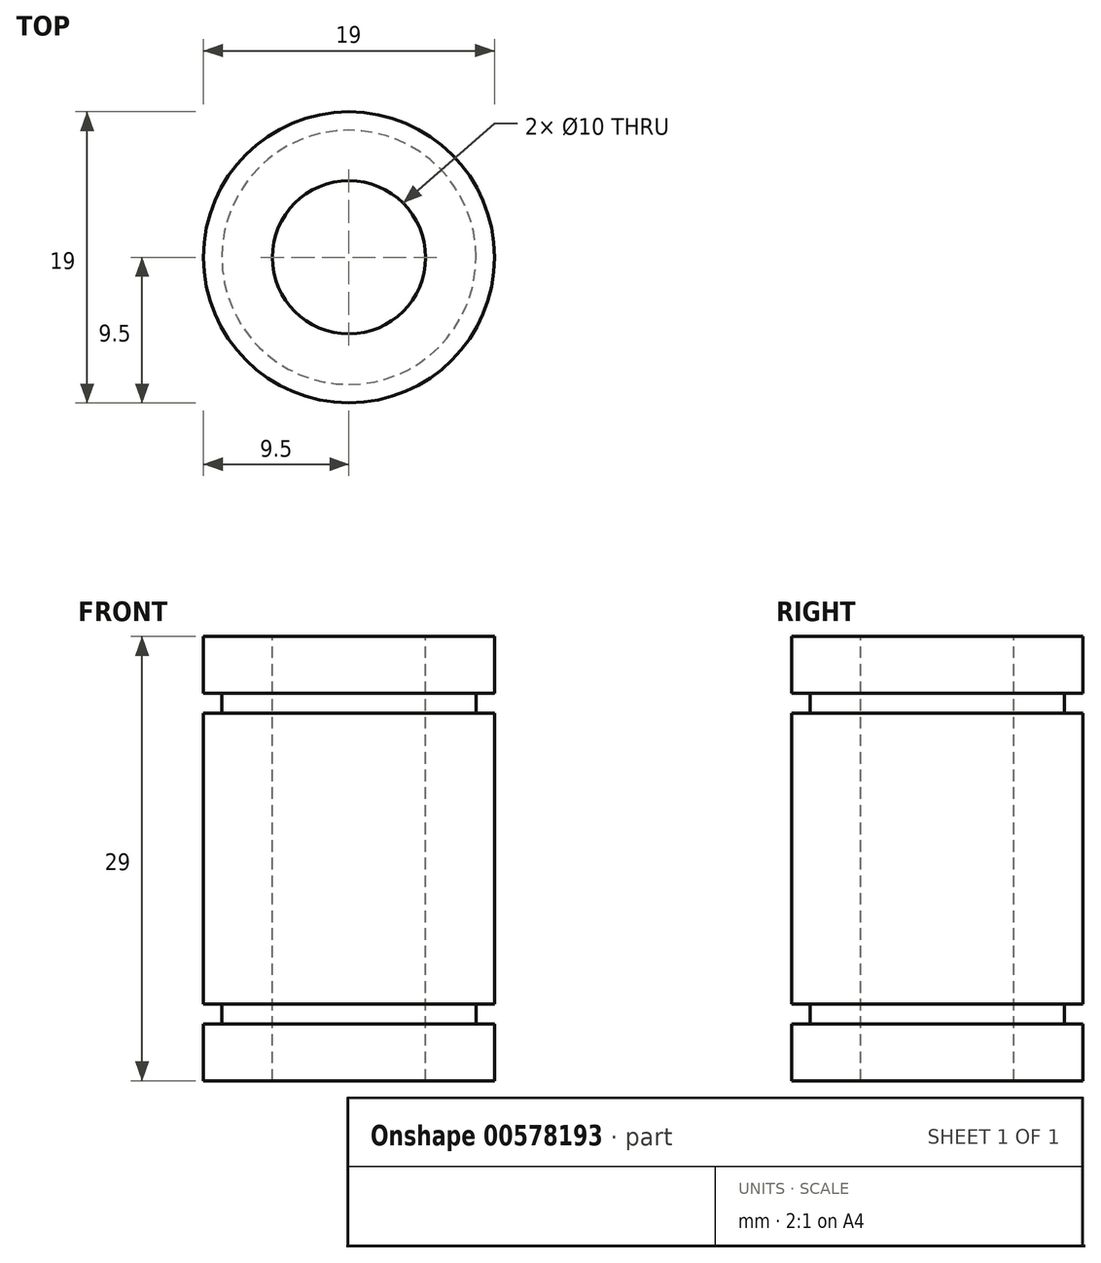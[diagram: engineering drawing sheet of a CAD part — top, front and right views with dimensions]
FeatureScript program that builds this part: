
annotation { "Feature Type Name" : "Feature", "Feature Type Description" : "" }
export const myFeature = defineFeature(function(context is Context, id is Id, definition is map)
    precondition{}
    {
        {
            var Q0;
            Q0=qCreatedBy(makeId("Front.planeOp"),FACE);
            var sketch = newSketch(context, id + "F0", { "sketchPlane" : qUnion([Q0])});
            skLineSegment(sketch, "E0", {"start": v(0, 14.5) * mm, "end": v(-9.5, 14.5) * mm});
            skLineSegment(sketch, "E1", {"start": v(-9.5, 14.5) * mm, "end": v(-9.5, 10.8) * mm});
            skLineSegment(sketch, "E2", {"start": v(-9.5, 10.8) * mm, "end": v(-8.3, 10.8) * mm});
            skLineSegment(sketch, "E3", {"start": v(-8.3, 10.8) * mm, "end": v(-8.3, 9.5) * mm});
            skLineSegment(sketch, "E4", {"start": v(-8.3, 9.5) * mm, "end": v(-9.5, 9.5) * mm});
            skLineSegment(sketch, "E5", {"start": v(-9.5, 9.5) * mm, "end": v(-9.5, 0) * mm});
            skLineSegment(sketch, "E6", {"start": v(-24.14, 0) * mm, "end": v(24.62, 0) * mm, "construction": true});
            skLineSegment(sketch, "E7.MirrorCS", {"start": v(0, -14.5) * mm, "end": v(-9.5, -14.5) * mm});
            skLineSegment(sketch, "E8.MirrorCS", {"start": v(-9.5, -14.5) * mm, "end": v(-9.5, -10.8) * mm});
            skLineSegment(sketch, "E9.MirrorCS", {"start": v(-9.5, -10.8) * mm, "end": v(-8.3, -10.8) * mm});
            skLineSegment(sketch, "E10.MirrorCS", {"start": v(-8.3, -10.8) * mm, "end": v(-8.3, -9.5) * mm});
            skLineSegment(sketch, "E11.MirrorCS", {"start": v(-8.3, -9.5) * mm, "end": v(-9.5, -9.5) * mm});
            skLineSegment(sketch, "E12.MirrorCS", {"start": v(-9.5, -9.5) * mm, "end": v(-9.5, 0) * mm});
            skLineSegment(sketch, "E13", {"start": v(0, 14.5) * mm, "end": v(0, 0) * mm});
            skLineSegment(sketch, "E14.MirrorCS", {"start": v(0, -14.5) * mm, "end": v(0, 0) * mm});
            skSolve(sketch);
        }
        {
            var Q0;
            Q0=makeQuery(id+"F0.imprint","IMPRINT",FACE,{"disambiguationData":[TD([[makeQuery(id+"F0.imprint","IMPRINT",EDGE,{"derivedFrom":sQuery(id+"F0.wireOp",EDGE,"E0")}),1.0]])]});
            var Q1;
            Q1=sQuery(id+"F0.wireOp",EDGE,"E13");
            revolve(context, id + "F1", {"entities" : qUnion([Q0]), "axis" : qUnion([Q1]), "revolveType" : RevolveType.FULL});
        }
        {
            var Q0;
            Q0=makeQuery(id+"F1.opRevolve","SWEPT_FACE",FACE,{"disambiguationData":[OSD([sQuery(id+"F0.wireOp",EDGE,"E0")])]});
            var sketch = newSketch(context, id + "F2", { "sketchPlane" : qUnion([Q0])});
            skPoint(sketch, "E15", {"position": v(0, 0) * mm});
            skSolve(sketch);
        }
        {
            var Q0;
            Q0=sQuery(id+"F2.wireOp",VERTEX,"E15");
            var Q1;
            Q1=makeQuery(id+"F1.opRevolve","SWEPT_BODY",BODY,{"disambiguationData":[OSD([sQuery(id+"F0.wireOp",EDGE,"E0"),sQuery(id+"F0.wireOp",EDGE,"E1"),sQuery(id+"F0.wireOp",EDGE,"E2"),sQuery(id+"F0.wireOp",EDGE,"E3"),sQuery(id+"F0.wireOp",EDGE,"E4"),sQuery(id+"F0.wireOp",EDGE,"E5"),sQuery(id+"F0.wireOp",EDGE,"E7.MirrorCS"),sQuery(id+"F0.wireOp",EDGE,"E8.MirrorCS"),sQuery(id+"F0.wireOp",EDGE,"E9.MirrorCS"),sQuery(id+"F0.wireOp",EDGE,"E10.MirrorCS"),sQuery(id+"F0.wireOp",EDGE,"E11.MirrorCS"),sQuery(id+"F0.wireOp",EDGE,"E12.MirrorCS"),sQuery(id+"F0.wireOp",EDGE,"E13"),sQuery(id+"F0.wireOp",EDGE,"E14.MirrorCS")])]});
            hole(context, id + "F3", {"style" : HoleStyle.SIMPLE, "endStyle" : HoleEndStyle.THROUGH, "holeDiameter" : 10 * mm, "isTappedThrough" : true, "tappedDepth" : 12 * mm, "tapClearance" : 3, "locations" : qUnion([Q0]), "scope" : qUnion([Q1])});
        }
        {
            var Q0;
            Q0=makeQuery(id+"F1.opRevolve","SWEPT_BODY",BODY,{"disambiguationData":[OSD([sQuery(id+"F0.wireOp",EDGE,"E0"),sQuery(id+"F0.wireOp",EDGE,"E1"),sQuery(id+"F0.wireOp",EDGE,"E2"),sQuery(id+"F0.wireOp",EDGE,"E3"),sQuery(id+"F0.wireOp",EDGE,"E4"),sQuery(id+"F0.wireOp",EDGE,"E5"),sQuery(id+"F0.wireOp",EDGE,"E7.MirrorCS"),sQuery(id+"F0.wireOp",EDGE,"E8.MirrorCS"),sQuery(id+"F0.wireOp",EDGE,"E9.MirrorCS"),sQuery(id+"F0.wireOp",EDGE,"E10.MirrorCS"),sQuery(id+"F0.wireOp",EDGE,"E11.MirrorCS"),sQuery(id+"F0.wireOp",EDGE,"E12.MirrorCS"),sQuery(id+"F0.wireOp",EDGE,"E13"),sQuery(id+"F0.wireOp",EDGE,"E14.MirrorCS")])]});
            transform(context, id + "F4", {"entities" : qUnion([Q0]), "transformType" : TransformType.TRANSLATION_3D, "dx" : 0 * mm, "dy" : 0 * mm, "dz" : 0 * mm, "makeCopy" : true});
        }
    });
